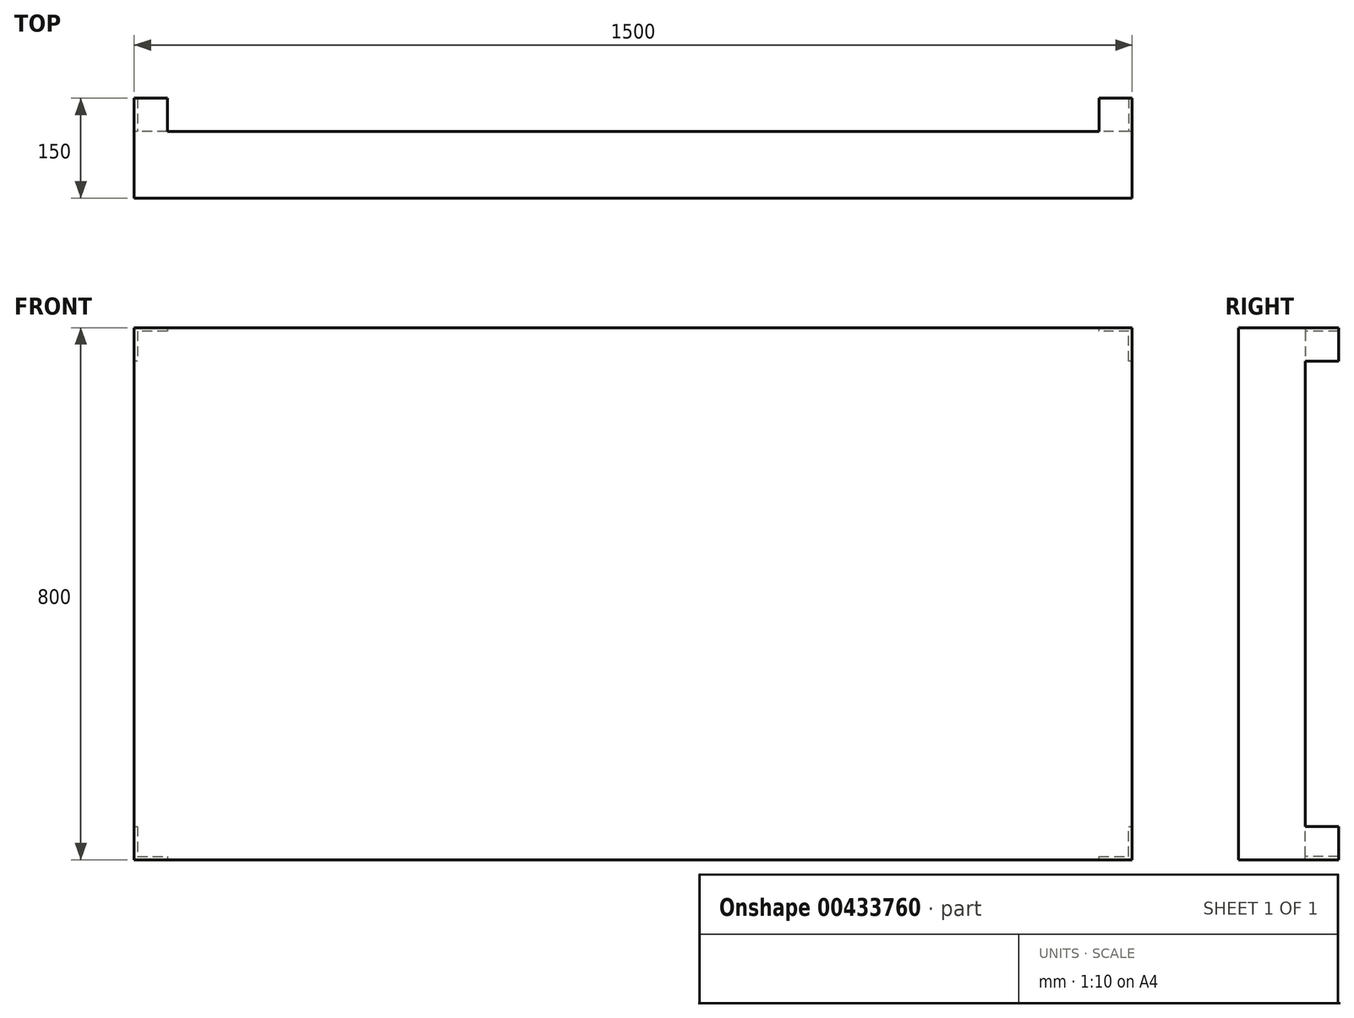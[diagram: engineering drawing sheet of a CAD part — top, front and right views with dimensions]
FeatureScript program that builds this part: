
annotation { "Feature Type Name" : "Feature", "Feature Type Description" : "" }
export const myFeature = defineFeature(function(context is Context, id is Id, definition is map)
    precondition{}
    {
        {
            var Q0;
            Q0=qCreatedBy(makeId("Front.planeOp"),FACE);
            var sketch = newSketch(context, id + "F0", { "sketchPlane" : qUnion([Q0])});
            skLineSegment(sketch, "E0.bottom", {"start": v(750, -400) * mm, "end": v(-750, -400) * mm});
            skLineSegment(sketch, "E0.top", {"start": v(750, 400) * mm, "end": v(-750, 400) * mm});
            skLineSegment(sketch, "E0.left", {"start": v(750, -400) * mm, "end": v(750, 400) * mm});
            skLineSegment(sketch, "E0.right", {"start": v(-750, -400) * mm, "end": v(-750, 400) * mm});
            skPoint(sketch, "E0.middle", {"position": v(0, 0) * mm});
            skSolve(sketch);
        }
        {
            var Q0;
            Q0=makeQuery(id+"F0.imprint","IMPRINT",FACE,{"disambiguationData":[TD([[makeQuery(id+"F0.imprint","IMPRINT",EDGE,{"derivedFrom":sQuery(id+"F0.wireOp",EDGE,"E0.bottom")}),-1.0]])]});
            extrude(context, id + "F1", {"entities" : qUnion([Q0]), "endBound" : BoundingType.SYMMETRIC, "depth" : 100 * mm});
        }
        {
            var Q0;
            Q0=makeQuery(id+"F1.opExtrude","CAP_FACE",FACE,{"disambiguationData":[OSD([sQuery(id+"F0.wireOp",EDGE,"E0.bottom"),sQuery(id+"F0.wireOp",EDGE,"E0.top"),sQuery(id+"F0.wireOp",EDGE,"E0.left"),sQuery(id+"F0.wireOp",EDGE,"E0.right")])],"isStart":true});
            var sketch = newSketch(context, id + "F2", { "sketchPlane" : qUnion([Q0])});
            skLineSegment(sketch, "E1", {"start": v(750, -400) * mm, "end": v(750, -350) * mm});
            skLineSegment(sketch, "E2", {"start": v(750, -400) * mm, "end": v(700, -400) * mm});
            skLineSegment(sketch, "E3", {"start": v(750, -350) * mm, "end": v(745, -350) * mm});
            skLineSegment(sketch, "E4", {"start": v(745, -350) * mm, "end": v(745, -395) * mm});
            skLineSegment(sketch, "E5", {"start": v(745, -395) * mm, "end": v(700, -395) * mm});
            skLineSegment(sketch, "E6", {"start": v(700, -395) * mm, "end": v(700, -400) * mm});
            skLineSegment(sketch, "E7", {"start": v(-750, -400) * mm, "end": v(-700, -400) * mm});
            skLineSegment(sketch, "E8", {"start": v(-750, -400) * mm, "end": v(-750, -350) * mm});
            skLineSegment(sketch, "E9", {"start": v(-700, -400) * mm, "end": v(-700, -395) * mm});
            skLineSegment(sketch, "E10", {"start": v(-700, -395) * mm, "end": v(-745, -395) * mm});
            skLineSegment(sketch, "E11", {"start": v(-745, -395) * mm, "end": v(-745, -350) * mm});
            skLineSegment(sketch, "E12", {"start": v(-745, -350) * mm, "end": v(-750, -350) * mm});
            skLineSegment(sketch, "E13", {"start": v(-750, 400) * mm, "end": v(-750, 350) * mm});
            skLineSegment(sketch, "E14", {"start": v(-750, 400) * mm, "end": v(-700, 400) * mm});
            skLineSegment(sketch, "E15", {"start": v(-750, 350) * mm, "end": v(-745, 350) * mm});
            skLineSegment(sketch, "E16", {"start": v(-745, 350) * mm, "end": v(-745, 395) * mm});
            skLineSegment(sketch, "E17", {"start": v(-745, 395) * mm, "end": v(-700, 395) * mm});
            skLineSegment(sketch, "E18", {"start": v(-700, 395) * mm, "end": v(-700, 400) * mm});
            skLineSegment(sketch, "E19", {"start": v(750, 400) * mm, "end": v(700, 400) * mm});
            skLineSegment(sketch, "E20", {"start": v(750, 400) * mm, "end": v(750, 350) * mm});
            skLineSegment(sketch, "E21", {"start": v(700, 400) * mm, "end": v(700, 395) * mm});
            skLineSegment(sketch, "E22", {"start": v(700, 395) * mm, "end": v(745, 395) * mm});
            skLineSegment(sketch, "E23", {"start": v(745, 395) * mm, "end": v(745, 350) * mm});
            skLineSegment(sketch, "E24", {"start": v(745, 350) * mm, "end": v(750, 350) * mm});
            skSolve(sketch);
        }
        {
            var Q0;
            Q0=makeQuery(id+"F2.imprint","IMPRINT",FACE,{"disambiguationData":[TD([[makeQuery(id+"F2.imprint","IMPRINT",EDGE,{"derivedFrom":sQuery(id+"F2.wireOp",EDGE,"E1")}),1.0]])]});
            var Q1;
            Q1=makeQuery(id+"F2.imprint","IMPRINT",FACE,{"disambiguationData":[TD([[makeQuery(id+"F2.imprint","IMPRINT",EDGE,{"derivedFrom":sQuery(id+"F2.wireOp",EDGE,"E7")}),1.0]])]});
            var Q2;
            Q2=makeQuery(id+"F2.imprint","IMPRINT",FACE,{"disambiguationData":[TD([[makeQuery(id+"F2.imprint","IMPRINT",EDGE,{"derivedFrom":sQuery(id+"F2.wireOp",EDGE,"E13")}),-1.0]])]});
            var Q3;
            Q3=makeQuery(id+"F2.imprint","IMPRINT",FACE,{"disambiguationData":[TD([[makeQuery(id+"F2.imprint","IMPRINT",EDGE,{"derivedFrom":sQuery(id+"F2.wireOp",EDGE,"E19")}),-1.0]])]});
            extrude(context, id + "F3", {"entities" : qUnion([Q0, Q1, Q2, Q3]), "operationType" : NewBodyOperationType.ADD, "depth" : 50 * mm});
        }
    });
